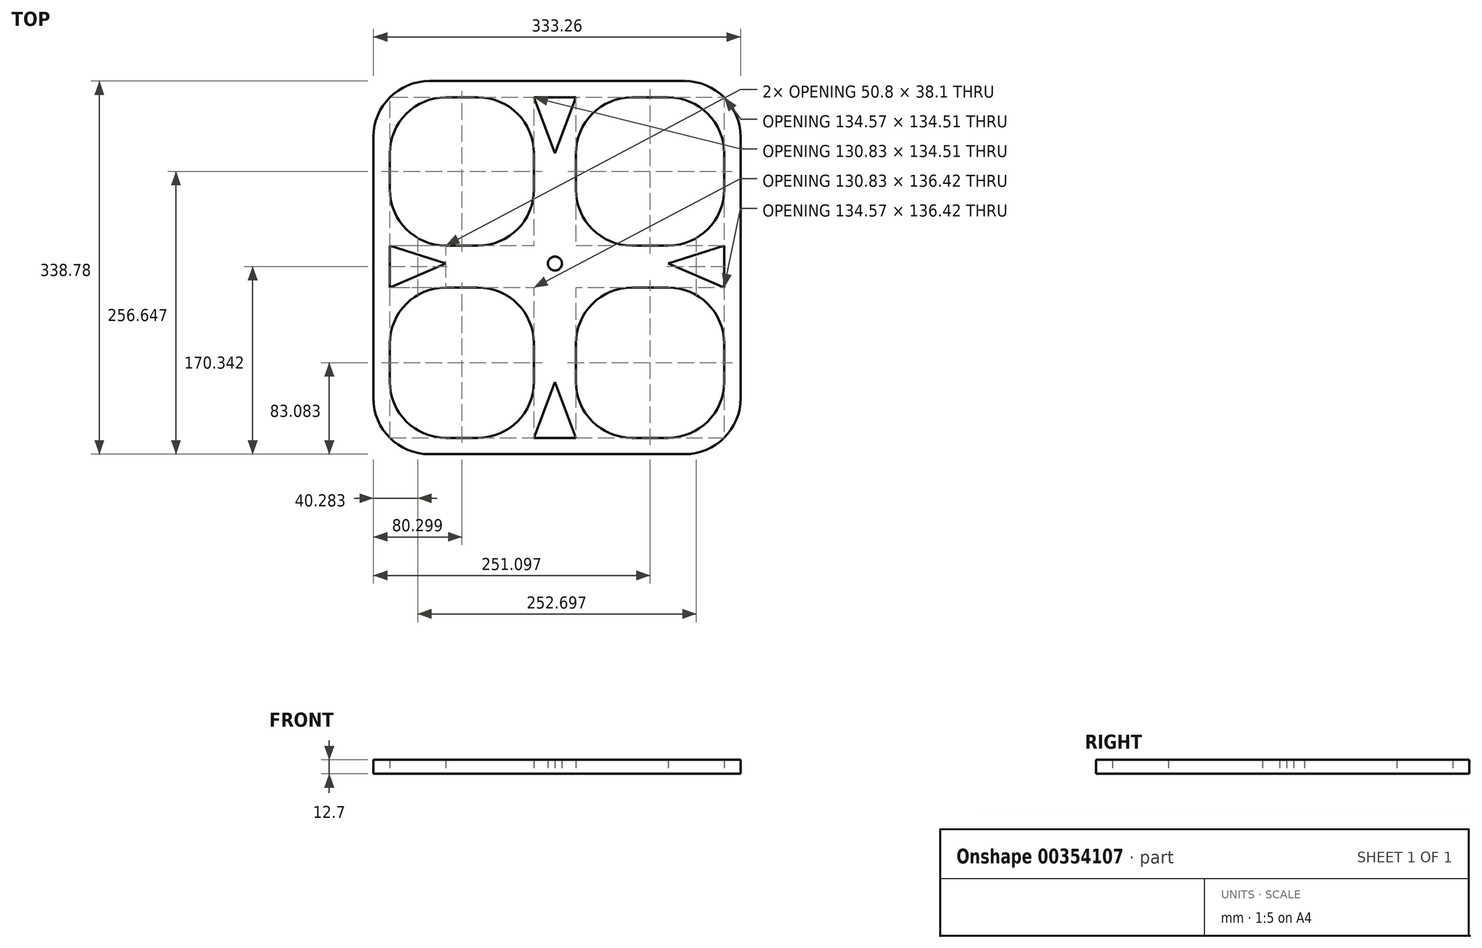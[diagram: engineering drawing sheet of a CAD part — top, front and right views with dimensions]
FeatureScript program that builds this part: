
annotation { "Feature Type Name" : "Feature", "Feature Type Description" : "" }
export const myFeature = defineFeature(function(context is Context, id is Id, definition is map)
    precondition{}
    {
        {
            var Q0;
            Q0=qCreatedBy(makeId("Top.planeOp"),FACE);
            var sketch = newSketch(context, id + "F0", { "sketchPlane" : qUnion([Q0])});
            skPoint(sketch, "E0.middle", {"position": v(1.32, 0.71) * mm});
            skCircle(sketch, "E1", {"center": v(1.32, 0.71) * mm, "radius": 6.35 * mm});
            skPoint(sketch, "E2.visualSharp", {"position": v(154.94, 17.07) * mm});
            skPoint(sketch, "E3.visualSharp", {"position": v(20.37, 151.58) * mm});
            skPoint(sketch, "E4.visualSharp", {"position": v(154.94, 151.58) * mm});
            skPoint(sketch, "E5.visualSharp", {"position": v(-148.56, 17.07) * mm});
            skPoint(sketch, "E6.visualSharp", {"position": v(-148.56, 151.58) * mm});
            skPoint(sketch, "E7.visualSharp", {"position": v(-17.73, 151.58) * mm});
            skPoint(sketch, "E8.visualSharp", {"position": v(-148.56, -157.45) * mm});
            skPoint(sketch, "E9.visualSharp", {"position": v(-17.73, -157.45) * mm});
            skPoint(sketch, "E10.visualSharp", {"position": v(-148.56, -21.03) * mm});
            skPoint(sketch, "E11.visualSharp", {"position": v(20.37, -157.45) * mm});
            skPoint(sketch, "E12.visualSharp", {"position": v(154.94, -157.45) * mm});
            skPoint(sketch, "E13.visualSharp", {"position": v(154.94, -21.03) * mm});
            skLineSegment(sketch, "E14", {"start": v(-112.64, -172.32) * mm, "end": v(119.02, -172.32) * mm});
            skLineSegment(sketch, "E15", {"start": v(169.82, -121.52) * mm, "end": v(169.82, 115.66) * mm});
            skLineSegment(sketch, "E16", {"start": v(119.02, 166.46) * mm, "end": v(-112.64, 166.46) * mm});
            skLineSegment(sketch, "E17", {"start": v(-163.44, 166.46) * mm, "end": v(-163.44, 158.42) * mm});
            skLineSegment(sketch, "E18", {"start": v(-163.44, -121.52) * mm, "end": v(-163.44, 115.66) * mm});
            skPoint(sketch, "E19.visualSharp", {"position": v(-163.44, 166.46) * mm});
            skArc(sketch, "E19.filletArc", {"start": v(-112.64, 166.46) * mm, "mid": v(-148.56, 151.58) * mm, "end": v(-163.44, 115.66) * mm});
            skPoint(sketch, "E20.visualSharp", {"position": v(169.82, 166.46) * mm});
            skArc(sketch, "E20.filletArc", {"start": v(169.82, 115.66) * mm, "mid": v(154.94, 151.58) * mm, "end": v(119.02, 166.46) * mm});
            skPoint(sketch, "E21.visualSharp", {"position": v(169.82, -172.32) * mm});
            skArc(sketch, "E21.filletArc", {"start": v(119.02, -172.32) * mm, "mid": v(154.94, -157.45) * mm, "end": v(169.82, -121.52) * mm});
            skPoint(sketch, "E22.visualSharp", {"position": v(-163.44, -172.32) * mm});
            skArc(sketch, "E22.filletArc", {"start": v(-163.44, -121.52) * mm, "mid": v(-148.56, -157.45) * mm, "end": v(-112.64, -172.32) * mm});
            skLineSegment(sketch, "E23", {"start": v(1.32, -106.65) * mm, "end": v(-17.73, -157.45) * mm});
            skLineSegment(sketch, "E24", {"start": v(20.37, -157.45) * mm, "end": v(-17.73, -157.45) * mm});
            skLineSegment(sketch, "E25", {"start": v(20.37, -157.45) * mm, "end": v(1.32, -106.65) * mm});
            skLineSegment(sketch, "E26", {"start": v(1.32, 100.78) * mm, "end": v(-17.73, 151.58) * mm});
            skLineSegment(sketch, "E27", {"start": v(-17.73, 151.58) * mm, "end": v(20.37, 151.58) * mm});
            skLineSegment(sketch, "E28", {"start": v(20.37, 151.58) * mm, "end": v(1.32, 100.78) * mm});
            skLineSegment(sketch, "E29", {"start": v(-148.56, 17.07) * mm, "end": v(-148.56, -21.03) * mm});
            skLineSegment(sketch, "E30", {"start": v(104.14, 0.71) * mm, "end": v(154.94, 17.07) * mm});
            skLineSegment(sketch, "E31", {"start": v(154.94, -21.03) * mm, "end": v(154.94, 17.07) * mm});
            skLineSegment(sketch, "E32", {"start": v(154.94, -21.03) * mm, "end": v(104.14, 0.71) * mm});
            skLineSegment(sketch, "E33", {"start": v(-97.76, 0.71) * mm, "end": v(-148.56, -21.03) * mm});
            skLineSegment(sketch, "E34", {"start": v(-148.56, 17.07) * mm, "end": v(-97.76, 0.71) * mm});
            skSolve(sketch);
        }
        {
            var Q0;
            Q0=makeQuery(id+"F0.imprint","IMPRINT",FACE,{"disambiguationData":[TD([[makeQuery(id+"F0.imprint","IMPRINT",EDGE,{"derivedFrom":sQuery(id+"F0.wireOp",EDGE,"E1")}),-1.0]])]});
            extrude(context, id + "F1", {"entities" : qUnion([Q0]), "depth" : 12.7 * mm});
        }
        {
            var Q0;
            Q0=makeQuery(id+"F1.opExtrude","SWEPT_BODY",BODY,{"disambiguationData":[OSD([sQuery(id+"F0.wireOp",EDGE,"E1"),sQuery(id+"F0.wireOp",EDGE,"E14"),sQuery(id+"F0.wireOp",EDGE,"E15"),sQuery(id+"F0.wireOp",EDGE,"E16"),sQuery(id+"F0.wireOp",EDGE,"E18"),sQuery(id+"F0.wireOp",EDGE,"E19.filletArc"),sQuery(id+"F0.wireOp",EDGE,"E20.filletArc"),sQuery(id+"F0.wireOp",EDGE,"E21.filletArc"),sQuery(id+"F0.wireOp",EDGE,"E22.filletArc"),sQuery(id+"F0.wireOp",EDGE,"E23"),sQuery(id+"F0.wireOp",EDGE,"E24"),sQuery(id+"F0.wireOp",EDGE,"E25"),sQuery(id+"F0.wireOp",EDGE,"E26"),sQuery(id+"F0.wireOp",EDGE,"E27"),sQuery(id+"F0.wireOp",EDGE,"E28"),sQuery(id+"F0.wireOp",EDGE,"E29"),sQuery(id+"F0.wireOp",EDGE,"E30"),sQuery(id+"F0.wireOp",EDGE,"E31"),sQuery(id+"F0.wireOp",EDGE,"E32"),sQuery(id+"F0.wireOp",EDGE,"E33"),sQuery(id+"F0.wireOp",EDGE,"E34")])]});
            deleteBodies(context, id + "F2", {"entities" : qUnion([Q0])});
        }
        {
            var Q0;
            Q0=qCreatedBy(makeId("Top.planeOp"),FACE);
            var sketch = newSketch(context, id + "F3", { "sketchPlane" : qUnion([Q0])});
            skLineSegment(sketch, "E35.bottom", {"start": v(104.14, 17.07) * mm, "end": v(71.17, 17.07) * mm});
            skLineSegment(sketch, "E35.top", {"start": v(104.14, -21.03) * mm, "end": v(71.17, -21.03) * mm});
            skPoint(sketch, "E35.middle", {"position": v(1.32, 0.71) * mm});
            skLineSegment(sketch, "E36.left", {"start": v(20.37, 100.78) * mm, "end": v(20.37, 67.87) * mm});
            skLineSegment(sketch, "E36.right", {"start": v(-17.73, 100.78) * mm, "end": v(-17.73, 67.87) * mm});
            skPoint(sketch, "E37", {"position": v(-17.73, 17.07) * mm});
            skPoint(sketch, "E38", {"position": v(20.37, 17.07) * mm});
            skPoint(sketch, "E39", {"position": v(20.37, -21.03) * mm});
            skPoint(sketch, "E40", {"position": v(-17.73, -21.03) * mm});
            skLineSegment(sketch, "E41.trimOffspring", {"start": v(-17.73, -71.83) * mm, "end": v(-17.73, -106.65) * mm});
            skLineSegment(sketch, "E42.trimOffspring", {"start": v(-68.53, 17.07) * mm, "end": v(-97.76, 17.07) * mm});
            skLineSegment(sketch, "E43.trimOffspring", {"start": v(20.37, -71.83) * mm, "end": v(20.37, -106.65) * mm});
            skLineSegment(sketch, "E44.trimOffspring", {"start": v(-68.53, -21.03) * mm, "end": v(-97.76, -21.03) * mm});
            skCircle(sketch, "E45", {"center": v(1.32, 0.71) * mm, "radius": 6.35 * mm});
            skArc(sketch, "E46.filletArc", {"start": v(-24.08, 17.07) * mm, "mid": v(-18.78, 19.92) * mm, "end": v(-18.23, 25.9) * mm});
            skArc(sketch, "E47.filletArc", {"start": v(-68.53, 17.07) * mm, "mid": v(-32.6, 31.95) * mm, "end": v(-17.73, 67.87) * mm});
            skArc(sketch, "E48.filletArc", {"start": v(20.37, 67.87) * mm, "mid": v(35.25, 31.95) * mm, "end": v(71.17, 17.07) * mm});
            skArc(sketch, "E49.filletArc", {"start": v(71.17, -21.03) * mm, "mid": v(35.25, -35.9) * mm, "end": v(20.37, -71.83) * mm});
            skArc(sketch, "E50.filletArc", {"start": v(-17.73, -71.83) * mm, "mid": v(-32.6, -35.9) * mm, "end": v(-68.53, -21.03) * mm});
            skLineSegment(sketch, "E51", {"start": v(71.17, 151.58) * mm, "end": v(104.14, 151.58) * mm});
            skLineSegment(sketch, "E52", {"start": v(154.94, 100.78) * mm, "end": v(154.94, 67.87) * mm});
            skPoint(sketch, "E53.visualSharp", {"position": v(154.94, 17.07) * mm});
            skArc(sketch, "E53.filletArc", {"start": v(104.14, 17.07) * mm, "mid": v(140.06, 31.95) * mm, "end": v(154.94, 67.87) * mm});
            skPoint(sketch, "E54.visualSharp", {"position": v(20.37, 151.58) * mm});
            skArc(sketch, "E54.filletArc", {"start": v(71.17, 151.58) * mm, "mid": v(35.25, 136.7) * mm, "end": v(20.37, 100.78) * mm});
            skPoint(sketch, "E55.visualSharp", {"position": v(154.94, 151.58) * mm});
            skArc(sketch, "E55.filletArc", {"start": v(154.94, 100.78) * mm, "mid": v(140.06, 136.7) * mm, "end": v(104.14, 151.58) * mm});
            skLineSegment(sketch, "E56", {"start": v(-148.56, 67.87) * mm, "end": v(-148.56, 100.78) * mm});
            skLineSegment(sketch, "E57", {"start": v(-97.76, 151.58) * mm, "end": v(-68.53, 151.58) * mm});
            skPoint(sketch, "E58.visualSharp", {"position": v(-148.56, 17.07) * mm});
            skArc(sketch, "E58.filletArc", {"start": v(-148.56, 67.87) * mm, "mid": v(-133.68, 31.95) * mm, "end": v(-97.76, 17.07) * mm});
            skPoint(sketch, "E59.visualSharp", {"position": v(-148.56, 151.58) * mm});
            skArc(sketch, "E59.filletArc", {"start": v(-97.76, 151.58) * mm, "mid": v(-133.68, 136.7) * mm, "end": v(-148.56, 100.78) * mm});
            skPoint(sketch, "E60.visualSharp", {"position": v(-17.73, 151.58) * mm});
            skArc(sketch, "E60.filletArc", {"start": v(-17.73, 100.78) * mm, "mid": v(-32.6, 136.7) * mm, "end": v(-68.53, 151.58) * mm});
            skLineSegment(sketch, "E61", {"start": v(-148.56, -71.83) * mm, "end": v(-148.56, -106.65) * mm});
            skLineSegment(sketch, "E62", {"start": v(-97.76, -157.45) * mm, "end": v(-68.53, -157.45) * mm});
            skPoint(sketch, "E63.visualSharp", {"position": v(-148.56, -157.45) * mm});
            skArc(sketch, "E63.filletArc", {"start": v(-148.56, -106.65) * mm, "mid": v(-133.68, -142.57) * mm, "end": v(-97.76, -157.45) * mm});
            skPoint(sketch, "E64.visualSharp", {"position": v(-17.73, -157.45) * mm});
            skPoint(sketch, "E65.visualSharp", {"position": v(-148.56, -21.03) * mm});
            skArc(sketch, "E65.filletArc", {"start": v(-97.76, -21.03) * mm, "mid": v(-133.68, -35.9) * mm, "end": v(-148.56, -71.83) * mm});
            skArc(sketch, "E66.filletArc", {"start": v(-68.53, -157.45) * mm, "mid": v(-32.6, -142.57) * mm, "end": v(-17.73, -106.65) * mm});
            skLineSegment(sketch, "E67", {"start": v(71.17, -157.45) * mm, "end": v(104.14, -157.45) * mm});
            skLineSegment(sketch, "E68", {"start": v(154.94, -106.65) * mm, "end": v(154.94, -71.83) * mm});
            skPoint(sketch, "E69.visualSharp", {"position": v(20.37, -157.45) * mm});
            skArc(sketch, "E69.filletArc", {"start": v(20.37, -106.65) * mm, "mid": v(35.25, -142.57) * mm, "end": v(71.17, -157.45) * mm});
            skPoint(sketch, "E70.visualSharp", {"position": v(154.94, -157.45) * mm});
            skArc(sketch, "E70.filletArc", {"start": v(104.14, -157.45) * mm, "mid": v(140.06, -142.57) * mm, "end": v(154.94, -106.65) * mm});
            skPoint(sketch, "E71.visualSharp", {"position": v(154.94, -21.03) * mm});
            skArc(sketch, "E71.filletArc", {"start": v(154.94, -71.83) * mm, "mid": v(140.06, -35.9) * mm, "end": v(104.14, -21.03) * mm});
            skLineSegment(sketch, "E72", {"start": v(-112.64, -172.32) * mm, "end": v(119.02, -172.32) * mm});
            skLineSegment(sketch, "E73", {"start": v(169.82, -121.52) * mm, "end": v(169.82, 115.66) * mm});
            skLineSegment(sketch, "E74", {"start": v(119.02, 166.46) * mm, "end": v(-112.64, 166.46) * mm});
            skLineSegment(sketch, "E75", {"start": v(-163.44, 166.46) * mm, "end": v(-163.44, 158.42) * mm});
            skLineSegment(sketch, "E76", {"start": v(-163.44, -121.52) * mm, "end": v(-163.44, 115.66) * mm});
            skPoint(sketch, "E77.visualSharp", {"position": v(-163.44, 166.46) * mm});
            skArc(sketch, "E77.filletArc", {"start": v(-112.64, 166.46) * mm, "mid": v(-148.56, 151.58) * mm, "end": v(-163.44, 115.66) * mm});
            skPoint(sketch, "E78.visualSharp", {"position": v(169.82, 166.46) * mm});
            skArc(sketch, "E78.filletArc", {"start": v(169.82, 115.66) * mm, "mid": v(154.94, 151.58) * mm, "end": v(119.02, 166.46) * mm});
            skPoint(sketch, "E79.visualSharp", {"position": v(169.82, -172.32) * mm});
            skArc(sketch, "E79.filletArc", {"start": v(119.02, -172.32) * mm, "mid": v(154.94, -157.45) * mm, "end": v(169.82, -121.52) * mm});
            skPoint(sketch, "E80.visualSharp", {"position": v(-163.44, -172.32) * mm});
            skArc(sketch, "E80.filletArc", {"start": v(-163.44, -121.52) * mm, "mid": v(-148.56, -157.45) * mm, "end": v(-112.64, -172.32) * mm});
            skLineSegment(sketch, "E81", {"start": v(1.32, -106.65) * mm, "end": v(-17.73, -157.45) * mm});
            skLineSegment(sketch, "E82", {"start": v(20.37, -157.45) * mm, "end": v(-17.73, -157.45) * mm});
            skLineSegment(sketch, "E83", {"start": v(20.37, -157.45) * mm, "end": v(1.32, -106.65) * mm});
            skLineSegment(sketch, "E84", {"start": v(1.32, 100.78) * mm, "end": v(-17.73, 151.58) * mm});
            skLineSegment(sketch, "E85", {"start": v(-17.73, 151.58) * mm, "end": v(20.37, 151.58) * mm});
            skLineSegment(sketch, "E86", {"start": v(20.37, 151.58) * mm, "end": v(1.32, 100.78) * mm});
            skLineSegment(sketch, "E87", {"start": v(-148.56, 17.07) * mm, "end": v(-148.56, -21.03) * mm});
            skLineSegment(sketch, "E88", {"start": v(104.14, 0.71) * mm, "end": v(154.94, 17.07) * mm});
            skLineSegment(sketch, "E89", {"start": v(154.94, -21.03) * mm, "end": v(154.94, 17.07) * mm});
            skLineSegment(sketch, "E90", {"start": v(154.94, -21.03) * mm, "end": v(104.14, 0.71) * mm});
            skLineSegment(sketch, "E91", {"start": v(-97.76, 0.71) * mm, "end": v(-148.56, -21.03) * mm});
            skLineSegment(sketch, "E92", {"start": v(-148.56, 17.07) * mm, "end": v(-97.76, 0.71) * mm});
            skSolve(sketch);
        }
        {
            var Q0;
            Q0=makeQuery(id+"F3.imprint","IMPRINT",FACE,{"disambiguationData":[TD([[makeQuery(id+"F3.imprint","IMPRINT",EDGE,{"derivedFrom":sQuery(id+"F3.wireOp",EDGE,"E35.bottom")}),1.0]])]});
            extrude(context, id + "F4", {"entities" : qUnion([Q0]), "depth" : 12.7 * mm});
        }
    });
